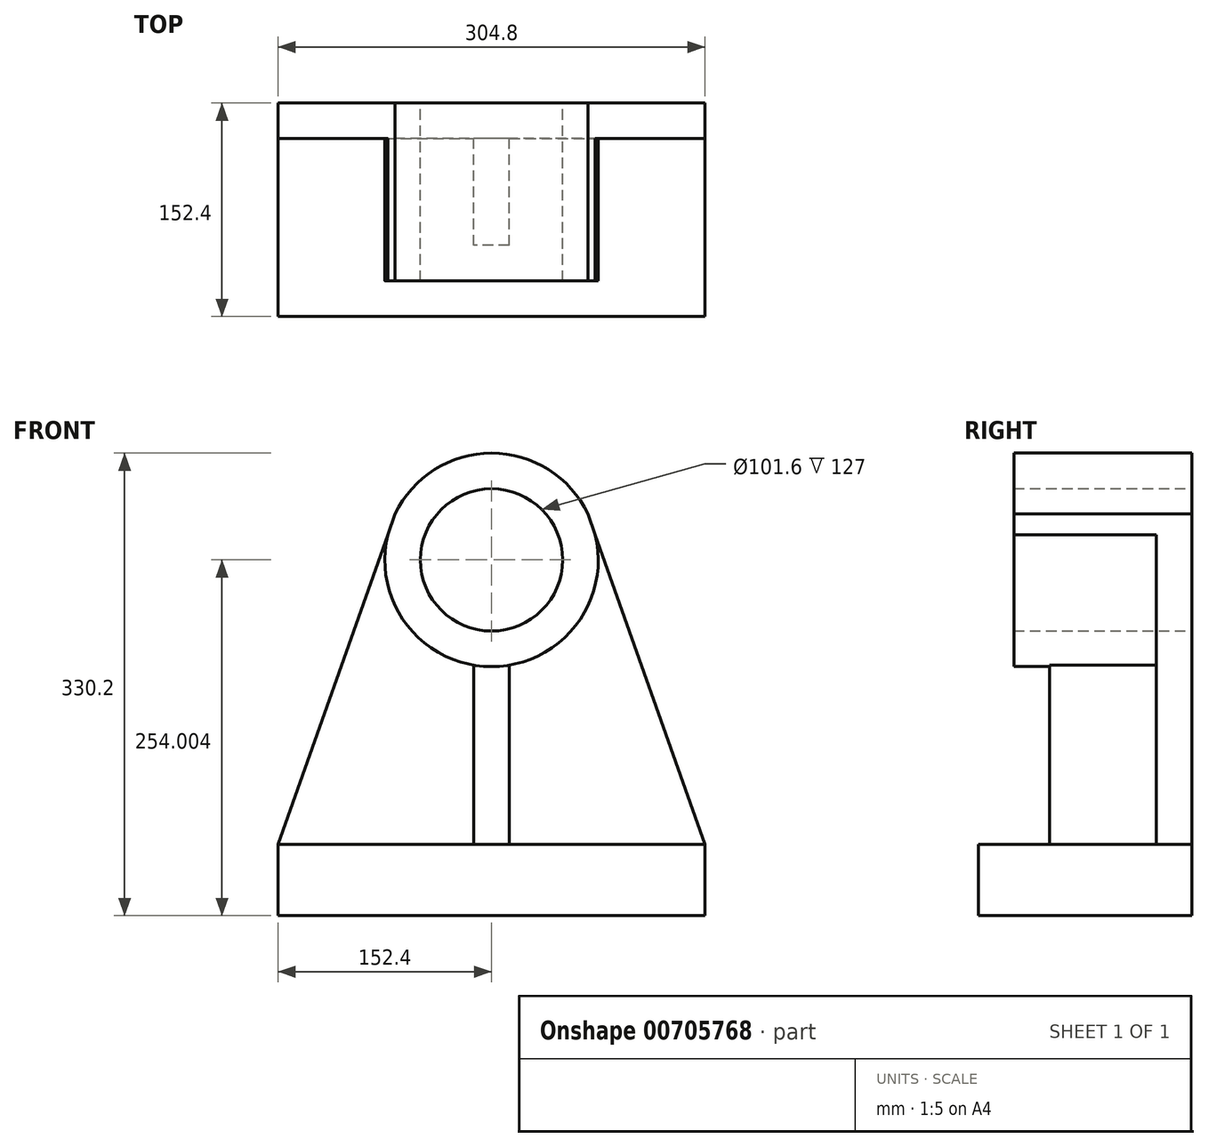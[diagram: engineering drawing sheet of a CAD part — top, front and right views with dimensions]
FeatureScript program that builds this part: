
annotation { "Feature Type Name" : "Feature", "Feature Type Description" : "" }
export const myFeature = defineFeature(function(context is Context, id is Id, definition is map)
    precondition{}
    {
        {
            var Q0;
            Q0=qCreatedBy(makeId("Front.planeOp"),FACE);
            var sketch = newSketch(context, id + "F0", { "sketchPlane" : qUnion([Q0])});
            skLineSegment(sketch, "E0", {"start": v(-152.4, -237.62) * mm, "end": v(152.4, -237.62) * mm});
            skLineSegment(sketch, "E1", {"start": v(152.4, -237.62) * mm, "end": v(152.4, -186.82) * mm});
            skLineSegment(sketch, "E2", {"start": v(152.4, -186.82) * mm, "end": v(-152.4, -186.82) * mm});
            skLineSegment(sketch, "E3", {"start": v(-152.4, -186.82) * mm, "end": v(-152.4, -237.62) * mm});
            skLineSegment(sketch, "E4", {"start": v(-152.4, -186.82) * mm, "end": v(-68.81, 49.11) * mm});
            skLineSegment(sketch, "E5", {"start": v(68.81, 49.11) * mm, "end": v(152.4, -186.82) * mm});
            skCircle(sketch, "E6", {"center": v(0, 16.38) * mm, "radius": 76.2 * mm});
            skPoint(sketch, "E6.centerSnap0", {"position": v(0, 49.11) * mm});
            skCircle(sketch, "E7", {"center": v(0, 16.38) * mm, "radius": 50.8 * mm});
            skSolve(sketch);
        }
        {
            var Q0;
            {var subQ0=sQuery(id+"F0.wireOp",EDGE,"E2");Q0=makeQuery(id+"F0.imprint","IMPRINT",FACE,{"disambiguationData":[TD([[makeQuery(id+"F0.imprint","IMPRINT",EDGE,{"derivedFrom":subQ0}),-1.0]])]});}
            extrude(context, id + "F1", {"entities" : qUnion([Q0]), "depth" : 25.4 * mm, "offsetDistance" : 25.4 * mm});
        }
        {
            var Q0;
            Q0=makeQuery(id+"F0.imprint","IMPRINT",FACE,{"disambiguationData":[TD([[makeQuery(id+"F0.imprint","IMPRINT",EDGE,{"derivedFrom":sQuery(id+"F0.wireOp",EDGE,"E0")}),1.0]])]});
            extrude(context, id + "F2", {"entities" : qUnion([Q0]), "operationType" : NewBodyOperationType.ADD, "depth" : 152.4 * mm, "offsetDistance" : 25.4 * mm});
        }
        {
            var Q0;
            Q0=makeQuery(id+"F0.imprint","IMPRINT",FACE,{"disambiguationData":[TD([[makeQuery(id+"F0.imprint","IMPRINT",EDGE,{"derivedFrom":sQuery(id+"F0.wireOp",EDGE,"E7")}),-1.0]])]});
            extrude(context, id + "F3", {"entities" : qUnion([Q0]), "operationType" : NewBodyOperationType.ADD, "depth" : 127 * mm, "offsetDistance" : 25.4 * mm});
        }
        {
            var Q0;
            Q0=qCreatedBy(makeId("Right.planeOp"),FACE);
            var sketch = newSketch(context, id + "F4", { "sketchPlane" : qUnion([Q0])});
            skPoint(sketch, "E8", {"position": v(-101.6, -47.23) * mm});
            skLineSegment(sketch, "E9", {"start": v(-101.6, -47.23) * mm, "end": v(-101.6, -186.8) * mm});
            skLineSegment(sketch, "E10", {"start": v(-101.6, -186.8) * mm, "end": v(-25.4, -186.8) * mm});
            skLineSegment(sketch, "E11", {"start": v(-101.6, -47.23) * mm, "end": v(-25.4, -47.23) * mm});
            skLineSegment(sketch, "E12", {"start": v(-25.4, -47.23) * mm, "end": v(-25.4, -186.8) * mm});
            skSolve(sketch);
        }
        {
            var Q0;
            Q0=makeQuery(id+"F4.imprint","IMPRINT",FACE,{"disambiguationData":[TD([[makeQuery(id+"F4.imprint","IMPRINT",EDGE,{"derivedFrom":sQuery(id+"F4.wireOp",EDGE,"E9")}),1.0]])]});
            extrude(context, id + "F5", {"entities" : qUnion([Q0]), "operationType" : NewBodyOperationType.ADD, "endBound" : BoundingType.SYMMETRIC, "depth" : 25.4 * mm, "offsetDistance" : 25.4 * mm});
        }
    });
